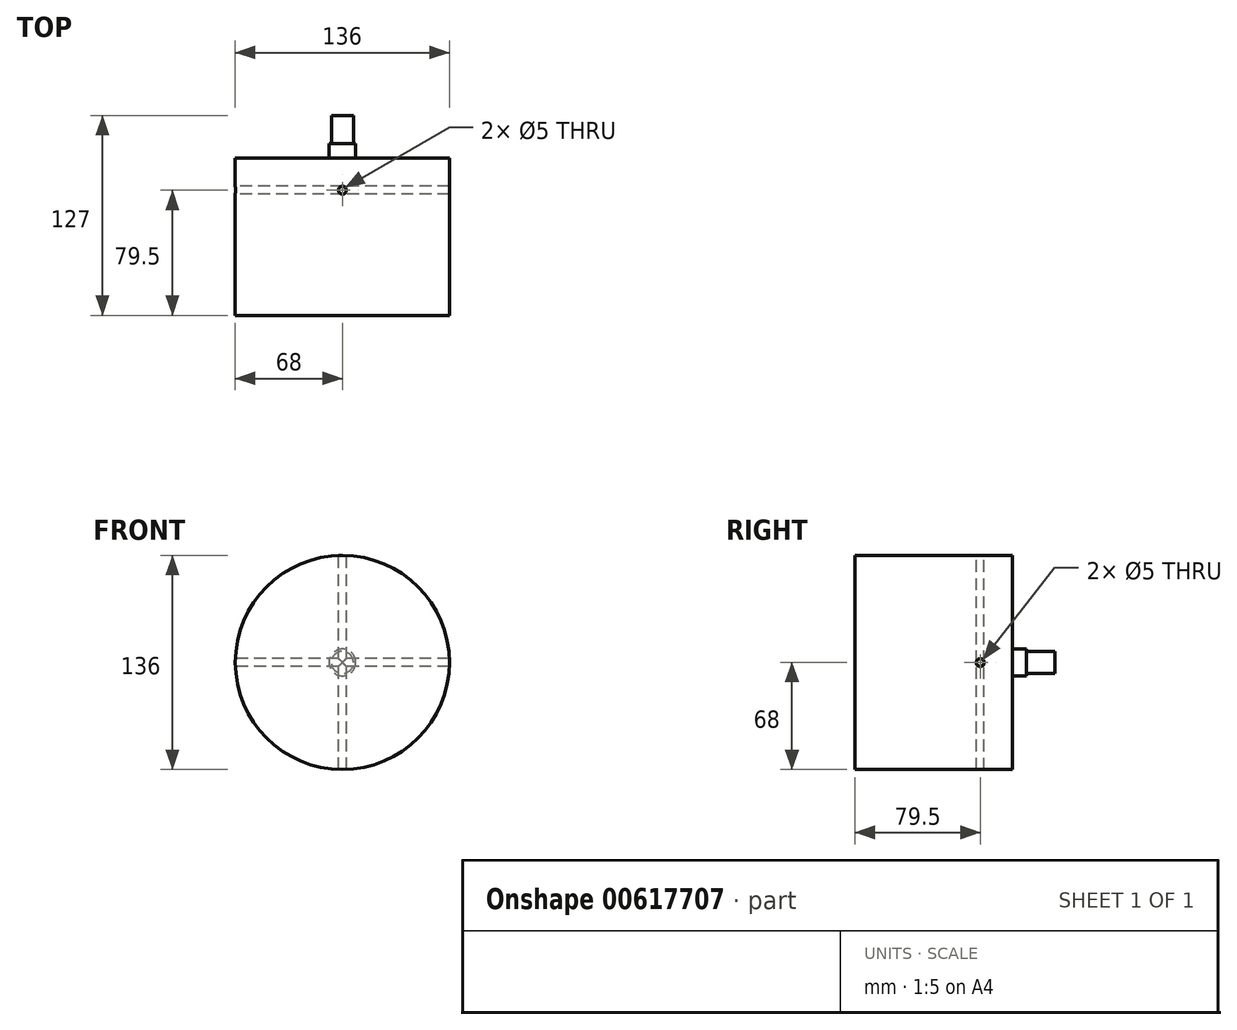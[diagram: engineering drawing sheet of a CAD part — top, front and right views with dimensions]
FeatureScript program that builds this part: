
annotation { "Feature Type Name" : "Feature", "Feature Type Description" : "" }
export const myFeature = defineFeature(function(context is Context, id is Id, definition is map)
    precondition{}
    {
        {
            var Q0;
            Q0=qCreatedBy(makeId("Front.planeOp"),FACE);
            var sketch = newSketch(context, id + "F0", { "sketchPlane" : qUnion([Q0])});
            skCircle(sketch, "E0", {"center": v(0, 0) * mm, "radius": 68 * mm});
            skCircle(sketch, "E1", {"center": v(0, 0) * mm, "radius": 8.5 * mm});
            skSolve(sketch);
        }
        {
            var Q0;
            Q0=makeQuery(id+"F0.imprint","IMPRINT",FACE,{"disambiguationData":[TD([[makeQuery(id+"F0.imprint","IMPRINT",EDGE,{"derivedFrom":sQuery(id+"F0.wireOp",EDGE,"E0")}),1.0]])]});
            var Q1;
            Q1=makeQuery(id+"F0.imprint","IMPRINT",FACE,{"disambiguationData":[TD([[makeQuery(id+"F0.imprint","IMPRINT",EDGE,{"derivedFrom":sQuery(id+"F0.wireOp",EDGE,"E1")}),1.0]])]});
            extrude(context, id + "F1", {"entities" : qUnion([Q0, Q1]), "depth" : 100 * mm, "offsetDistance" : 25 * mm});
        }
        {
            var Q0;
            Q0=makeQuery(id+"F0.imprint","IMPRINT",FACE,{"disambiguationData":[TD([[makeQuery(id+"F0.imprint","IMPRINT",EDGE,{"derivedFrom":sQuery(id+"F0.wireOp",EDGE,"E1")}),1.0]])]});
            extrude(context, id + "F2", {"entities" : qUnion([Q0]), "operationType" : NewBodyOperationType.ADD, "oppositeDirection" : true, "depth" : 9 * mm, "offsetDistance" : 25 * mm});
        }
        {
            var Q0;
            Q0=makeQuery(id+"F2.opExtrude","CAP_FACE",FACE,{"disambiguationData":[OSD([sQuery(id+"F0.wireOp",EDGE,"E1")])],"isStart":false});
            var sketch = newSketch(context, id + "F3", { "sketchPlane" : qUnion([Q0])});
            skCircle(sketch, "E2", {"center": v(0, 0) * mm, "radius": 7 * mm});
            skSolve(sketch);
        }
        {
            var Q0;
            Q0=qCreatedBy(makeId("Top.planeOp"),FACE);
            var sketch = newSketch(context, id + "F4", { "sketchPlane" : qUnion([Q0])});
            skCircle(sketch, "E3", {"center": v(0, -20.5) * mm, "radius": 2.5 * mm});
            skSolve(sketch);
        }
        {
            var Q0;
            Q0=makeQuery(id+"F4.imprint","IMPRINT",FACE,{"disambiguationData":[TD([[makeQuery(id+"F4.imprint","IMPRINT",EDGE,{"derivedFrom":sQuery(id+"F4.wireOp",EDGE,"E3")}),1.0]])]});
            extrude(context, id + "F5", {"entities" : qUnion([Q0]), "operationType" : NewBodyOperationType.REMOVE, "endBound" : BoundingType.SYMMETRIC, "oppositeDirection" : true, "depth" : 150 * mm, "offsetDistance" : 25 * mm});
        }
        {
            var Q0;
            Q0=qCreatedBy(makeId("Right.planeOp"),FACE);
            var sketch = newSketch(context, id + "F6", { "sketchPlane" : qUnion([Q0])});
            skCircle(sketch, "E4", {"center": v(-20.5, 0) * mm, "radius": 2.5 * mm});
            skSolve(sketch);
        }
        {
            var Q0;
            Q0 = qSketchRegion(id + "F6", true);
            extrude(context, id + "F7", {"entities" : qUnion([Q0]), "operationType" : NewBodyOperationType.REMOVE, "endBound" : BoundingType.SYMMETRIC, "depth" : 150 * mm, "offsetDistance" : 25 * mm});
        }
        {
            var Q0;
            Q0=makeQuery(id+"F3.imprint","IMPRINT",FACE,{"disambiguationData":[TD([[makeQuery(id+"F3.imprint","IMPRINT",EDGE,{"derivedFrom":sQuery(id+"F3.wireOp",EDGE,"E2")}),1.0]])]});
            extrude(context, id + "F8", {"entities" : qUnion([Q0]), "operationType" : NewBodyOperationType.ADD, "depth" : 18 * mm, "offsetDistance" : 25 * mm});
        }
    });
